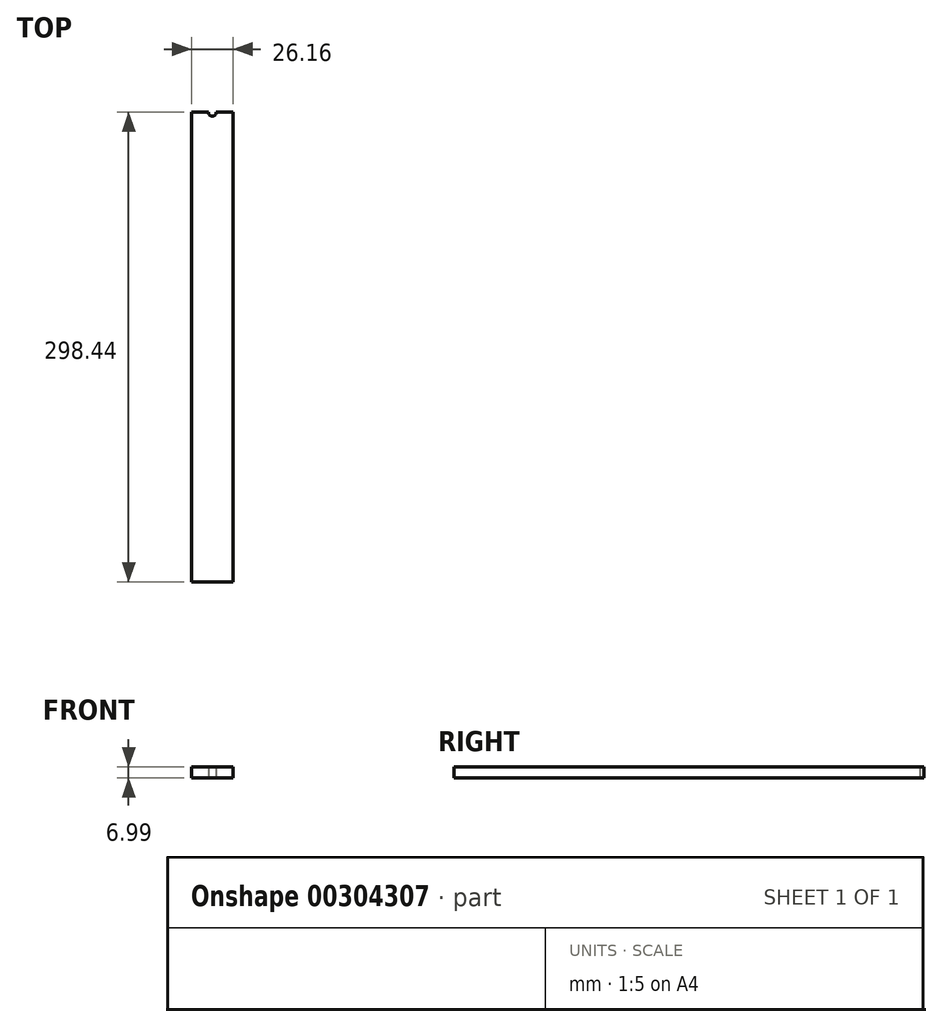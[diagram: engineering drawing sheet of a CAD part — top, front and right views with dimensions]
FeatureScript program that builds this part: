
annotation { "Feature Type Name" : "Feature", "Feature Type Description" : "" }
export const myFeature = defineFeature(function(context is Context, id is Id, definition is map)
    precondition{}
    {
        {
            var Q0;
            Q0=qCreatedBy(makeId("Top.planeOp"),FACE);
            var sketch = newSketch(context, id + "F0", { "sketchPlane" : qUnion([Q0])});
            skLineSegment(sketch, "E0.bottom", {"start": v(13.08, 149.23) * mm, "end": v(-13.08, 149.23) * mm});
            skLineSegment(sketch, "E0.top", {"start": v(13.08, -149.23) * mm, "end": v(-13.08, -149.23) * mm});
            skLineSegment(sketch, "E0.left", {"start": v(13.08, 149.23) * mm, "end": v(13.08, -149.22) * mm});
            skLineSegment(sketch, "E0.right", {"start": v(-13.08, 149.23) * mm, "end": v(-13.08, -149.22) * mm});
            skPoint(sketch, "E0.middle", {"position": v(0, 0) * mm});
            skLineSegment(sketch, "E1.bottom", {"start": v(-13.08, 149.23) * mm, "end": v(13.08, 149.23) * mm});
            skLineSegment(sketch, "E1.top", {"start": v(-13.08, 161.93) * mm, "end": v(13.08, 161.93) * mm});
            skLineSegment(sketch, "E1.left", {"start": v(-13.08, 149.23) * mm, "end": v(-13.08, 161.93) * mm});
            skLineSegment(sketch, "E1.right", {"start": v(13.08, 149.23) * mm, "end": v(13.08, 161.93) * mm});
            skLineSegment(sketch, "E2.bottom", {"start": v(-13.08, -149.23) * mm, "end": v(13.08, -149.23) * mm});
            skLineSegment(sketch, "E2.top", {"start": v(-13.08, -161.92) * mm, "end": v(13.08, -161.92) * mm});
            skLineSegment(sketch, "E2.left", {"start": v(-13.08, -149.23) * mm, "end": v(-13.08, -161.92) * mm});
            skLineSegment(sketch, "E2.right", {"start": v(13.08, -149.23) * mm, "end": v(13.08, -161.92) * mm});
            skPoint(sketch, "E3", {"position": v(0, 149.23) * mm});
            skCircle(sketch, "E4", {"center": v(0, 149.23) * mm, "radius": 2.54 * mm});
            skSolve(sketch);
        }
        {
            var Q0;
            Q0=makeQuery(id+"F0.imprint","IMPRINT",FACE,{"disambiguationData":[TD([[makeQuery(id+"F0.imprint","IMPRINT",EDGE,{"derivedFrom":sQuery(id+"F0.wireOp",EDGE,"E0.left")}),-1.0]])]});
            var Q1;
            Q1=makeQuery(id+"F0.imprint","IMPRINT",FACE,{"disambiguationData":[TD([[makeQuery(id+"F0.imprint","IMPRINT",EDGE,{"derivedFrom":sQuery(id+"F0.wireOp",EDGE,"E1.bottom")}),1.0]])]});
            var Q2;
            Q2=makeQuery(id+"F0.imprint","IMPRINT",FACE,{"disambiguationData":[TD([[makeQuery(id+"F0.imprint","IMPRINT",EDGE,{"derivedFrom":sQuery(id+"F0.wireOp",EDGE,"E2.bottom")}),-1.0]])]});
            extrude(context, id + "F1", {"entities" : qUnion([Q0, Q1, Q2]), "depth" : 7 * mm});
        }
    });
